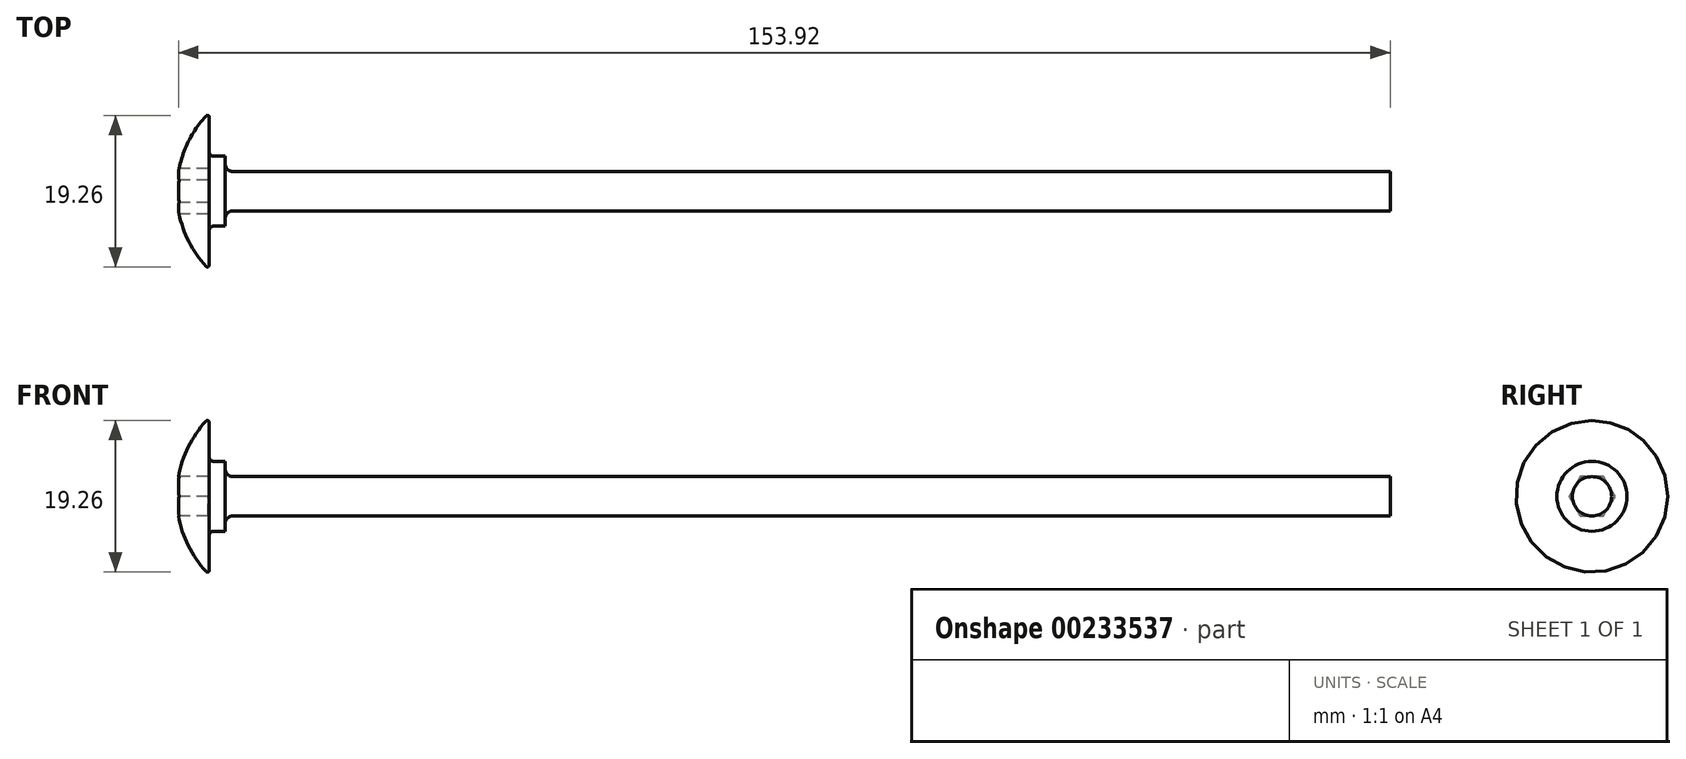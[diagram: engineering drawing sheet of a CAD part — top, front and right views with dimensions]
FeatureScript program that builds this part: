
annotation { "Feature Type Name" : "Feature", "Feature Type Description" : "" }
export const myFeature = defineFeature(function(context is Context, id is Id, definition is map)
    precondition{}
    {
        {
            var Q0;
            Q0=qCreatedBy(makeId("Top.planeOp"),FACE);
            var sketch = newSketch(context, id + "F0", { "sketchPlane" : qUnion([Q0])});
            skLineSegment(sketch, "E0", {"start": v(-82.6, 0) * mm, "end": v(154.14, 0) * mm, "construction": true});
            skLineSegment(sketch, "E1", {"start": v(154.14, 0) * mm, "end": v(154.14, 2.5) * mm});
            skLineSegment(sketch, "E2", {"start": v(154.14, 2.5) * mm, "end": v(6.14, 2.5) * mm});
            skLineSegment(sketch, "E3", {"start": v(4.14, 4.45) * mm, "end": v(4.14, 10) * mm});
            skLineSegment(sketch, "E4", {"start": v(4.14, 10) * mm, "end": v(16.1, 21.96) * mm, "construction": true});
            skLineSegment(sketch, "E5", {"start": v(0, 0) * mm, "end": v(0, -9.73) * mm, "construction": true});
            skArc(sketch, "E6", {"start": v(0, 0) * mm, "mid": v(1.08, 5.41) * mm, "end": v(4.14, 10) * mm});
            skLineSegment(sketch, "E7", {"start": v(4.14, 4.45) * mm, "end": v(6.14, 4.45) * mm});
            skLineSegment(sketch, "E8", {"start": v(6.14, 4.45) * mm, "end": v(6.14, 2.5) * mm});
            skPoint(sketch, "E9.orphan", {"position": v(4.14, 2.5) * mm});
            skLineSegment(sketch, "E10", {"start": v(0, 0) * mm, "end": v(154.14, 0) * mm});
            skSolve(sketch);
        }
        {
            var Q0;
            Q0=qSketchRegion(id+"F0",true);
            var Q1;
            Q1=sQuery(id+"F0.wireOp",EDGE,"E0");
            revolve(context, id + "F1", {"entities" : qUnion([Q0]), "axis" : qUnion([Q1]), "revolveType" : RevolveType.FULL});
        }
        {
            var Q0;
            Q0=makeQuery(id+"F1.opRevolve","SWEPT_EDGE",EDGE,{"disambiguationData":[OSD([sQuery(id+"F0.wireOp",EDGE,"E3"),sQuery(id+"F0.wireOp",EDGE,"E6")])]});
            fillet(context, id + "F2", {"entities" : qUnion([Q0]), "radius" : 0.25 * mm, "tangentPropagation" : true, "allowEdgeOverflow" : false});
        }
        {
            var Q0;
            Q0=makeQuery(id+"F1.opRevolve","SWEPT_EDGE",EDGE,{"disambiguationData":[OSD([sQuery(id+"F0.wireOp",EDGE,"E3"),sQuery(id+"F0.wireOp",EDGE,"E7")])]});
            fillet(context, id + "F3", {"entities" : qUnion([Q0]), "radius" : 0.5 * mm, "tangentPropagation" : true, "allowEdgeOverflow" : false});
        }
        {
            var Q0;
            Q0=makeQuery(id+"F1.opRevolve","SWEPT_EDGE",EDGE,{"disambiguationData":[OSD([sQuery(id+"F0.wireOp",EDGE,"E2"),sQuery(id+"F0.wireOp",EDGE,"E8")])]});
            fillet(context, id + "F4", {"entities" : qUnion([Q0]), "radius" : 1 * mm, "tangentPropagation" : true, "allowEdgeOverflow" : false});
        }
        {
            var Q0;
            Q0=qCreatedBy(makeId("Right.planeOp"),FACE);
            var sketch = newSketch(context, id + "F5", { "sketchPlane" : qUnion([Q0])});
            skCircle(sketch, "E11.cCircle", {"center": v(0, 0) * mm, "radius": 2.5 * mm, "construction": true});
            skLineSegment(sketch, "E11.0", {"start": v(-1.44, -2.5) * mm, "end": v(-2.89, 0) * mm});
            skLineSegment(sketch, "E11.1", {"start": v(-2.89, 0) * mm, "end": v(-1.44, 2.5) * mm});
            skLineSegment(sketch, "E11.2", {"start": v(-1.44, 2.5) * mm, "end": v(1.44, 2.5) * mm});
            skLineSegment(sketch, "E11.3", {"start": v(1.44, 2.5) * mm, "end": v(2.89, 0) * mm});
            skLineSegment(sketch, "E11.4", {"start": v(2.89, 0) * mm, "end": v(1.44, -2.5) * mm});
            skLineSegment(sketch, "E11.5", {"start": v(1.44, -2.5) * mm, "end": v(-1.44, -2.5) * mm});
            skPoint(sketch, "E11.0.midPoint", {"position": v(-2.17, -1.25) * mm});
            skLineSegment(sketch, "E12", {"start": v(13.73, 0) * mm, "end": v(-17.19, 0) * mm, "construction": true});
            skLineSegment(sketch, "E13", {"start": v(0, 17.1) * mm, "end": v(0, -13.72) * mm, "construction": true});
            skSolve(sketch);
        }
        {
            var Q0;
            Q0=qSketchRegion(id+"F5",true);
            extrude(context, id + "F6", {"entities" : qUnion([Q0]), "operationType" : NewBodyOperationType.REMOVE, "depth" : 4 * mm});
        }
    });
